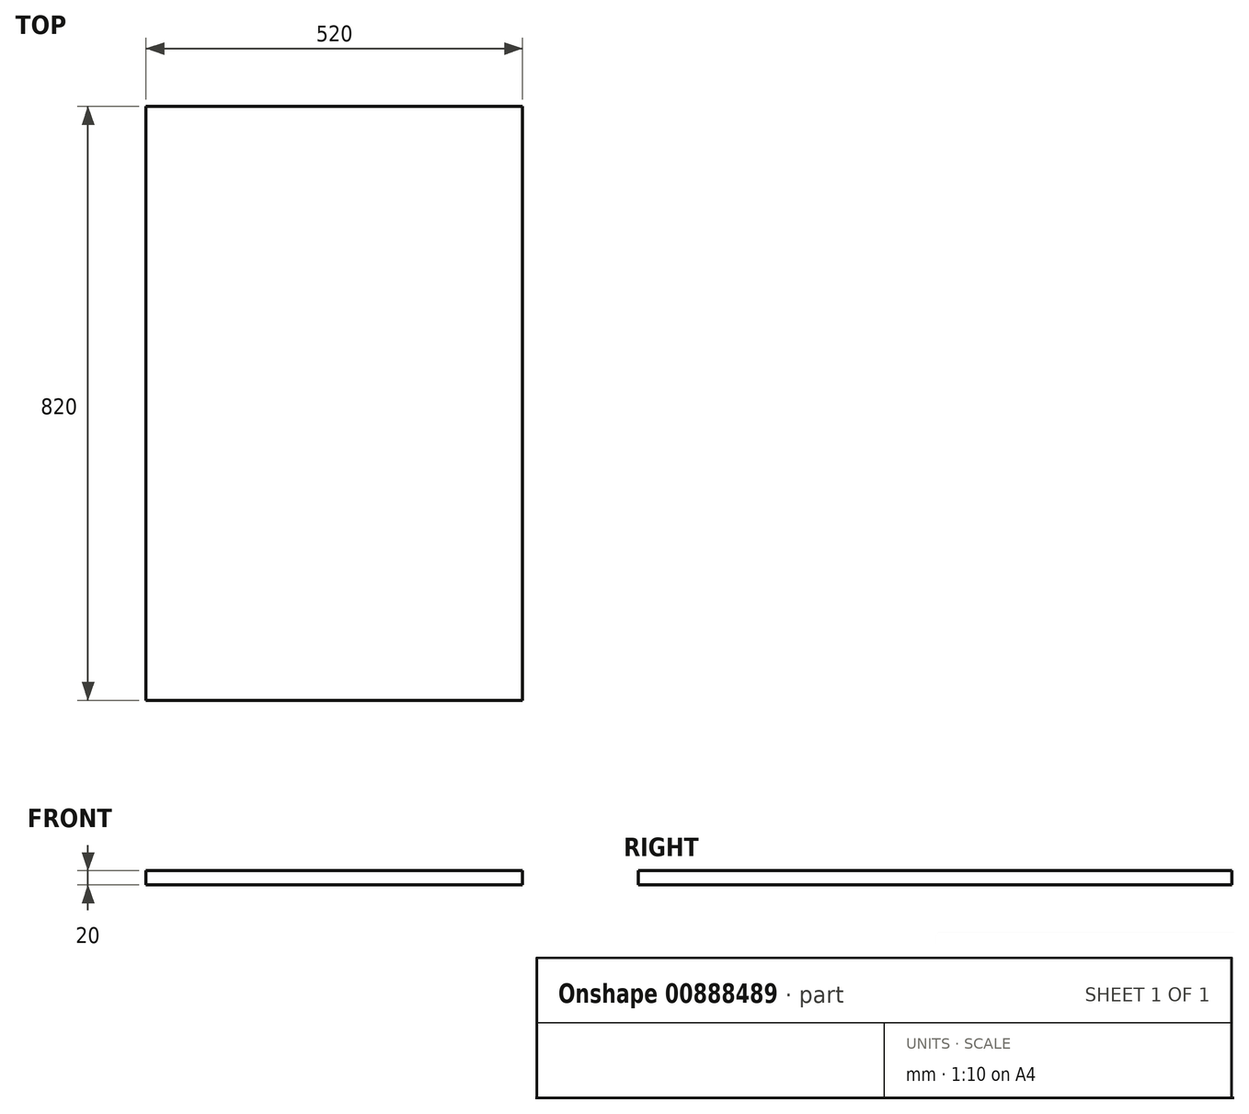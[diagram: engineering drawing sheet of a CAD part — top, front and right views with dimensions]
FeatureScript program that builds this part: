
annotation { "Feature Type Name" : "Feature", "Feature Type Description" : "" }
export const myFeature = defineFeature(function(context is Context, id is Id, definition is map)
    precondition{}
    {
        {
            var Q0;
            Q0=qCreatedBy(makeId("Top.planeOp"),FACE);
            var sketch = newSketch(context, id + "F0", { "sketchPlane" : qUnion([Q0])});
            skLineSegment(sketch, "E0.bottom", {"start": v(260, 410) * mm, "end": v(-260, 410) * mm});
            skLineSegment(sketch, "E0.top", {"start": v(260, -410) * mm, "end": v(-260, -410) * mm});
            skLineSegment(sketch, "E0.left", {"start": v(260, 410) * mm, "end": v(260, -410) * mm});
            skLineSegment(sketch, "E0.right", {"start": v(-260, 410) * mm, "end": v(-260, -410) * mm});
            skPoint(sketch, "E0.middle", {"position": v(0, 0) * mm});
            skSolve(sketch);
        }
        {
            var Q0;
            Q0 = qSketchRegion(id + "F0", true);
            extrude(context, id + "F1", {"entities" : qUnion([Q0]), "depth" : 20 * mm, "offsetDistance" : 25 * mm});
        }
    });
